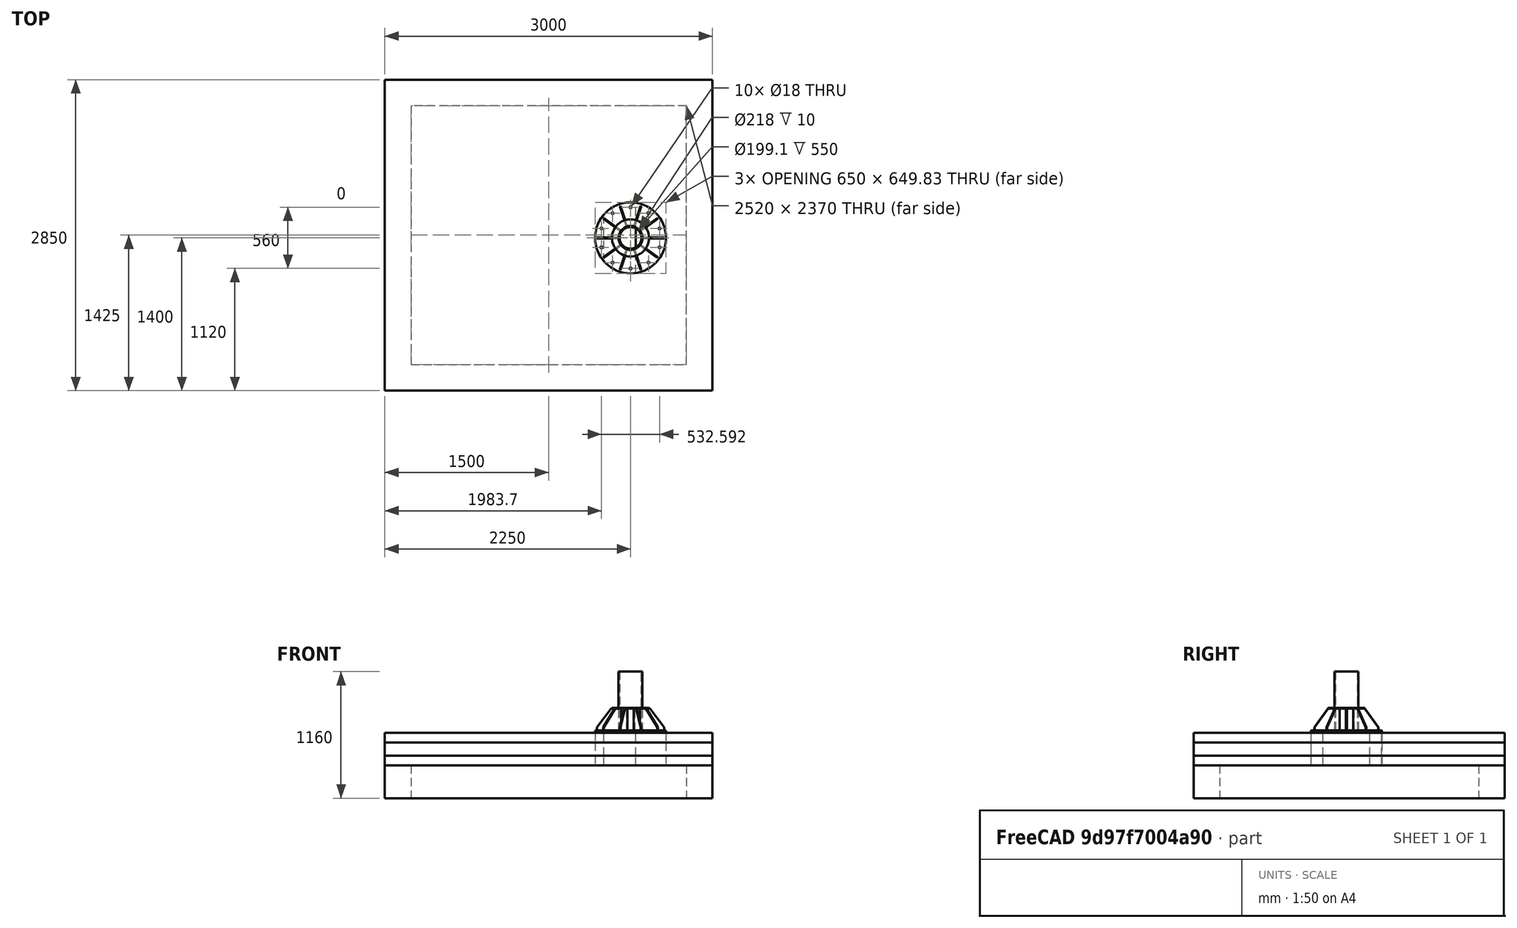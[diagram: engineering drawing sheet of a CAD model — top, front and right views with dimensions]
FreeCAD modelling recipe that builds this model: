
FCSTD DOCUMENT  (FreeCAD 0.21R33694 (Git))
Label: B_Parkaue_LIC_Betonplatte
License: All rights reserved
LicenseURL: http://en.wikipedia.org/wiki/All_rights_reserved
objects: Part::FeaturePython×12, Sketcher::SketchObject×7, Part::Extrusion×7, App::MaterialObjectPython×4, Image::ImagePlane×3, App::DocumentObjectGroup×3, Fem::ConstraintForce×3, Fem::FeaturePython×2, Part::MultiFuse×1, Part::Compound×1, Fem::FemMeshObjectPython×1, Fem::FemSolverObjectPython×1, Fem::ConstraintFixed×1, Fem::FemAnalysis×1
note: 28 computed .brp shape members not serialized (recipe doc carries the construction recipe); baked Part::Feature solids carry a one-line shape summary decoded from their .brp

FEATURE [Sketcher::SketchObject] Sketch
  FullyConstrained = true
  sketch-geometry (3):
    g0: Circle CenterX=0 CenterY=0 CenterZ=0 NormalX=0 NormalY=0 NormalZ=1 AngleXU=0 Radius=109.55
    g1: Circle CenterX=0 CenterY=0 CenterZ=0 NormalX=0 NormalY=0 NormalZ=1 AngleXU=0 Radius=99.55
    g2: LineSegment StartX=99.55 StartY=0 StartZ=0 EndX=109.55 EndY=0 EndZ=0
  constraints (8):
    c: Coincident(g0,g-1)
    c: Diameter(g0) = 219.1
    c: Coincident(g1,g0)
    c: PointOnObject(g2,g1)
    c: PointOnObject(g2,g0)
    c: PointOnObject(g2,g-1)
    c: Horizontal(g2)
    c: DistanceX(g2,g2) = 10
FEATURE [Part::Extrusion] Extrude  label="R219"
  Base = -> Sketch
  Dir = (0,0,1)
  DirMode = 0
  FaceMakerClass = Part::FaceMakerBullseye
  LengthFwd = 550
  LengthRev = 0
  Placement = pos=(0,0,10) rot=(0,0,1;0rad)
  Solid = true
  Symmetric = false
FEATURE [Part::FeaturePython] Flangia  # WARN: FeaturePython — macro-defined, semantics opaque (R4)
  AttacherType = Attacher::AttachEngine3D
  D = 650
  FlangeType = SO
  Kv = 0
  ODp = 0
  PRating = DIN-PN16
  PSize = DN250
  PType = Flange
  Ports = (2) [(0,0,0),(0,0,20)]
  d = 218
  df = 560
  drf = 0
  dwn = 0
  f = 18
  n = 10
  t = 20
  trf = 0
  twn = 0
FEATURE [Sketcher::SketchObject] Sketch002
  ExternalGeometry = -> [Flangia,Extrude]
  FullyConstrained = true
  Placement = pos=(0,0,0) rot=(1,0,0;1.5708rad)
  sketch-geometry (7):
    g0: LineSegment StartX=306.55 StartY=20 StartZ=0 EndX=120.692 EndY=20 EndZ=0
    g1: LineSegment StartX=120.692 StartY=20 StartZ=0 EndX=106.55 EndY=34.1421 EndZ=0
    g2: LineSegment StartX=106.55 StartY=34.1421 StartZ=0 EndX=106.55 EndY=205.858 EndZ=0
    g3: LineSegment StartX=106.55 StartY=205.858 StartZ=0 EndX=120.692 EndY=220 EndZ=0
    g4: LineSegment StartX=120.692 StartY=220 StartZ=0 EndX=176.55 EndY=220 EndZ=0
    g5: LineSegment StartX=176.55 StartY=220 StartZ=0 EndX=306.55 EndY=50 EndZ=0
    g6: LineSegment StartX=306.55 StartY=50 StartZ=0 EndX=306.55 EndY=20 EndZ=0
  constraints (21):
    c: Horizontal(g0)
    c: Coincident(g0,g1)
    c: Coincident(g1,g2)
    c: Vertical(g2)
    c: Coincident(g2,g3)
    c: Coincident(g3,g4)
    c: Horizontal(g4)
    c: Coincident(g4,g5)
    c: Coincident(g5,g6)
    c: Coincident(g6,g0)
    c: Vertical(g6)
    c: Horizontal(g0,g-3)
    c: Angle(g0,g1) = 2.35619
    c: Angle(g3,g4) = 2.35619
    c: Equal(g1,g3)
    c: DistanceX(g1,g-4) = 3
    c: Distance(g3) = 20
    c: DistanceX(g2,g4) = 70
    c: DistanceY(g6,g6) = 30
    c: DistanceY(g0,g4) = 200
    c: DistanceX(g1,g0) = 200
FEATURE [Part::Extrusion] Extrude002
  Base = -> Sketch002
  Dir = (0,-1,2e-16)
  DirMode = 2
  FaceMakerClass = Part::FaceMakerBullseye
  LengthFwd = 8
  LengthRev = 0
  Solid = true
  Symmetric = true
FEATURE [Part::FeaturePython] Array  label="Steifen"  # Draft array (typed FeaturePython)
  Angle = 360
  ArrayType = 1
  Axis = (0,0,1)
  Base = -> Extrude002
  Center = (0,0,0)
  Count = 8
  Fuse = false
  IntervalAxis = (0,0,0)
  IntervalX = (50,0,0)
  IntervalY = (0,50,0)
  IntervalZ = (0,0,50)
  NumberCircles = 3
  NumberPolar = 10
  NumberX = 2
  NumberY = 2
  NumberZ = 1
  RadialDistance = 50
  Symmetry = 1
  TangentialDistance = 25
FEATURE [Sketcher::SketchObject] Sketch003
  FullyConstrained = true
  MapMode = 5
  Placement = pos=(0,4.84e-14,220) rot=(0,0,1;0rad)
  Support = -> [Array]
  sketch-geometry (2):
    g0: Circle CenterX=0 CenterY=0 CenterZ=0 NormalX=0 NormalY=0 NormalZ=1 AngleXU=0 Radius=170
    g1: Circle CenterX=0 CenterY=0 CenterZ=0 NormalX=0 NormalY=0 NormalZ=1 AngleXU=0 Radius=104.5
  constraints (4):
    c: Coincident(g0,g-1)
    c: Coincident(g1,g0)
    c: Diameter(g1) = 209
    c: Diameter(g0) = 340
FEATURE [Part::Extrusion] Extrude003  label="Ringsteife"
  Base = -> Sketch003
  Dir = (0,2e-16,1)
  DirMode = 2
  FaceMakerClass = Part::FaceMakerBullseye
  LengthFwd = 6
  LengthRev = 0
  Solid = true
  Symmetric = false
FEATURE [Part::MultiFuse] Fusion  label="mast_fixing"
  Refine = true
  Shapes = -> [Extrude,Flangia,Array,Extrude003]
FEATURE [Image::ImagePlane] ImagePlane001  label="building"
  Placement = pos=(3085,400,-150) rot=(0,0,1;0rad)
  XSize = 13211.6
  YSize = 11768.8
  expr: XSize = 259.33 * 50.945 mm
  expr: YSize = 231.01 * 50.945 mm
FEATURE [Sketcher::SketchObject] Sketch005
  FullyConstrained = true
  sketch-geometry (4):
    g0: LineSegment StartX=-2250 StartY=1450 StartZ=0 EndX=750 EndY=1450 EndZ=0
    g1: LineSegment StartX=750 StartY=1450 StartZ=0 EndX=750 EndY=-1400 EndZ=0
    g2: LineSegment StartX=750 StartY=-1400 StartZ=0 EndX=-2250 EndY=-1400 EndZ=0
    g3: LineSegment StartX=-2250 StartY=-1400 StartZ=0 EndX=-2250 EndY=1450 EndZ=0
  constraints (12):
    c: Coincident(g0,g1)
    c: Coincident(g1,g2)
    c: Coincident(g2,g3)
    c: Coincident(g3,g0)
    c: Horizontal(g0)
    c: Horizontal(g2)
    c: Vertical(g1)
    c: Vertical(g3)
    c: DistanceX(g2,g2) = 3000
    c: DistanceY(g1,g-1) = 1400
    c: DistanceX(g-1,g1) = 750
    c: DistanceY(g3,g3) = 2850
FEATURE [Part::Extrusion] Extrude005  label="plate"
  Base = -> Sketch005
  Dir = (0,0,-1)
  DirMode = 0
  FaceMakerClass = Part::FaceMakerBullseye
  LengthFwd = 300
  LengthRev = 0
  Solid = true
  Symmetric = false
FEATURE [Sketcher::SketchObject] Sketch006
  FullyConstrained = true
  MapMode = 5
  Support = -> [Extrude005]
  sketch-geometry (7):
    g0: ArcOfCircle CenterX=0 CenterY=0 CenterZ=0 NormalX=0 NormalY=0 NormalZ=1 AngleXU=0 Radius=325 StartAngle=4.85928 EndAngle=7.70709
    g1: LineSegment StartX=0 StartY=0 StartZ=0 EndX=47.5684 EndY=321.5 EndZ=0
    g2: LineSegment StartX=47.5684 StartY=321.5 StartZ=0 EndX=47.5684 EndY=-321.5 EndZ=0
    g3: ArcOfCircle CenterX=0 CenterY=0 CenterZ=0 NormalX=0 NormalY=0 NormalZ=1 AngleXU=0 Radius=325 StartAngle=2.41667 EndAngle=3.86651
    g4: LineSegment StartX=-243.279 StartY=215.5 StartZ=0 EndX=-243.279 EndY=-215.5 EndZ=0
    g5: ArcOfCircle CenterX=0 CenterY=7.85e-14 CenterZ=0 NormalX=0 NormalY=0 NormalZ=1 AngleXU=0 Radius=325 StartAngle=3.86651 EndAngle=4.85928
    g6: ArcOfCircle CenterX=1.314e-13 CenterY=-3.469e-13 CenterZ=0 NormalX=0 NormalY=0 NormalZ=1 AngleXU=0 Radius=325 StartAngle=1.4239 EndAngle=2.41667
  constraints (20):
    c: Coincident(g0,g-1)
    c: Vertical(g0,g0)
    c: Coincident(g1,g0)
    c: Coincident(g1,g0)
    c: Coincident(g2,g0)
    c: Coincident(g2,g0)
    c: Diameter(g0) = 650
    c: Coincident(g3,g0)
    c: Vertical(g3,g3)
    c: Equal(g0,g3)
    c: Coincident(g4,g3)
    c: Coincident(g4,g3)
    c: DistanceY(g2,g2) = 643
    c: DistanceY(g4,g4) = 431
    c: PointOnObject(g5,g-2)
    c: Coincident(g5,g3)
    c: Coincident(g5,g0)
    c: Coincident(g6,g3)
    c: Coincident(g6,g0)
    c: Equal(g6,g0)
FEATURE [Sketcher::SketchObject] Sketch008
  ExternalGeometry = -> [Extrude005]
  FullyConstrained = true
  MapMode = 5
  Placement = pos=(0,0,-300) rot=(1,0,0;3.14159rad)
  Support = -> [Extrude005]
  sketch-geometry (12):
    g0: LineSegment StartX=-2250 StartY=1400 StartZ=0 EndX=750 EndY=1400 EndZ=0
    g1: LineSegment StartX=750 StartY=1400 StartZ=0 EndX=750 EndY=-1450 EndZ=0
    g2: LineSegment StartX=750 StartY=-1450 StartZ=0 EndX=-2250 EndY=-1450 EndZ=0
    g3: LineSegment StartX=-2250 StartY=-1450 StartZ=0 EndX=-2250 EndY=1400 EndZ=0
    g4: LineSegment StartX=-2010 StartY=1160 StartZ=0 EndX=510 EndY=1160 EndZ=0
    g5: LineSegment StartX=510 StartY=1160 StartZ=0 EndX=510 EndY=-1210 EndZ=0
    g6: LineSegment StartX=510 StartY=-1210 StartZ=0 EndX=-2010 EndY=-1210 EndZ=0
    g7: LineSegment StartX=-2010 StartY=-1210 StartZ=0 EndX=-2010 EndY=1160 EndZ=0
    g8: LineSegment StartX=-2010 StartY=1160 StartZ=0 EndX=-2010 EndY=1400 EndZ=0
    g9: LineSegment StartX=510 StartY=1160 StartZ=0 EndX=750 EndY=1160 EndZ=0
    g10: LineSegment StartX=-2010 StartY=-1210 StartZ=0 EndX=-2010 EndY=-1450 EndZ=0
    g11: LineSegment StartX=-2010 StartY=1160 StartZ=0 EndX=-2250 EndY=1160 EndZ=0
  constraints (34):
    c: Coincident(g0,g1)
    c: Coincident(g1,g2)
    c: Coincident(g2,g3)
    c: Coincident(g3,g0)
    c: Horizontal(g0)
    c: Horizontal(g2)
    c: Vertical(g1)
    c: Vertical(g3)
    c: Coincident(g0,g-3)
    c: Coincident(g1,g-4)
    c: Coincident(g4,g5)
    c: Coincident(g5,g6)
    c: Coincident(g6,g7)
    c: Coincident(g7,g4)
    c: Horizontal(g4)
    c: Horizontal(g6)
    c: Vertical(g5)
    c: Vertical(g7)
    c: Coincident(g8,g4)
    c: PointOnObject(g8,g0)
    c: Vertical(g8)
    c: Coincident(g9,g4)
    c: PointOnObject(g9,g1)
    c: Horizontal(g9)
    c: Equal(g8,g9)
    c: Coincident(g10,g6)
    c: PointOnObject(g10,g2)
    c: Vertical(g10)
    c: Coincident(g11,g4)
    c: PointOnObject(g11,g3)
    c: Horizontal(g11)
    c: Equal(g11,g8)
    c: Equal(g9,g10)
    c: DistanceX(g9,g9) = 240
FEATURE [Part::Extrusion] Extrude009  label="wall_masonry"
  Base = -> Sketch008
  Dir = (0,0,-1)
  DirMode = 2
  FaceMakerClass = Part::FaceMakerBullseye
  LengthFwd = 300
  LengthRev = 0
  Solid = true
  Symmetric = false
FEATURE [Image::ImagePlane] ImagePlane  label="top_view"
  Placement = pos=(32,-830,-100) rot=(0,0,1;0rad)
  XSize = 5389.33
  YSize = 4906.39
  expr: XSize = 206.67 * 26.077 mm
  expr: YSize = 188.15 * 26.077 mm
FEATURE [Image::ImagePlane] ImagePlane002  label="ansicht_yz"
  Placement = pos=(-2572,-300,2633) rot=(0.57735,0.57735,0.57735;2.0944rad)
  XSize = 4807.43
  YSize = 6945.54
  expr: XSize = 184.44 * 26.065 mm
  expr: YSize = 266.47 * 26.065 mm
FEATURE [App::DocumentObjectGroup] Group  label="drawings"
  Group = -> [ImagePlane001,ImagePlane,ImagePlane002]
FEATURE [Part::Extrusion] Extrude010  label="slice_loadFaces"
  Base = -> Sketch006
  Dir = (0,0,1)
  DirMode = 2
  FaceMakerClass = Part::FaceMakerBullseye
  LengthFwd = 100
  LengthRev = 400
  Solid = false
  Symmetric = false
FEATURE [Sketcher::SketchObject] Sketch009
  ExternalGeometry = -> [Extrude005]
  FullyConstrained = true
  Placement = pos=(0,0,0) rot=(1,0,0;1.5708rad)
  sketch-geometry (6):
    g0: LineSegment StartX=-2250 StartY=-45 StartZ=0 EndX=750 EndY=-45 EndZ=0
    g1: LineSegment StartX=-2250 StartY=-255 StartZ=0 EndX=750 EndY=-255 EndZ=0
    g2: LineSegment StartX=-2350 StartY=-210 StartZ=0 EndX=850 EndY=-210 EndZ=0
    g3: LineSegment StartX=-2350 StartY=-90 StartZ=0 EndX=850 EndY=-90 EndZ=0
    g4: LineSegment StartX=750 StartY=-255 StartZ=0 EndX=850 EndY=-210 EndZ=0
    g5: LineSegment StartX=750 StartY=-45 StartZ=0 EndX=850 EndY=-90 EndZ=0
  constraints (20):
    c: Horizontal(g0)
    c: Horizontal(g1)
    c: PointOnObject(g0,g-4)
    c: PointOnObject(g1,g-4)
    c: PointOnObject(g0,g-3)
    c: PointOnObject(g1,g-3)
    c: DistanceY(g-3,g1) = 45
    c: DistanceY(g0,g-3) = 45
    c: Horizontal(g2)
    c: Horizontal(g3)
    c: Equal(g3,g2)
    c: Vertical(g2,g3)
    c: DistanceX(g3,g-4) = 100
    c: DistanceX(g-3,g3) = 100
    c: Coincident(g4,g1)
    c: Coincident(g4,g2)
    c: Coincident(g5,g0)
    c: Coincident(g5,g3)
    c: Equal(g4,g5)
    c: DistanceY(g1,g2) = 45
FEATURE [Part::Extrusion] Extrude011  label="slice_Q524"
  Base = -> Sketch009
  Dir = (0,-1,-3e-16)
  DirMode = 2
  FaceMakerClass = Part::FaceMakerBullseye
  LengthFwd = 3200
  LengthRev = 0
  Solid = false
  Symmetric = true
FEATURE [Part::FeaturePython] Slice  # WARN: FeaturePython — macro-defined, semantics opaque (R4)
  Base = -> Extrude005
  Mode = 1
  Tolerance = 0
  Tools = -> [Extrude010]
FEATURE [Part::FeaturePython] Slice_child0  label="plate_rest_not_used"  # WARN: FeaturePython — macro-defined, semantics opaque (R4)
  Base = -> Slice
  FilterType = 1
  Invert = false
  OverrideMaxVal = 0
  WindowFrom = 80
  WindowTo = 100
  items = 0
FEATURE [Part::FeaturePython] Slice_child1  label="mast_neutral"  # WARN: FeaturePython — macro-defined, semantics opaque (R4)
  Base = -> Slice
  FilterType = 1
  Invert = false
  OverrideMaxVal = 0
  WindowFrom = 80
  WindowTo = 100
  items = 1
FEATURE [Part::FeaturePython] Slice_child2  label="mast_Z"  # WARN: FeaturePython — macro-defined, semantics opaque (R4)
  Base = -> Slice
  FilterType = 1
  Invert = false
  OverrideMaxVal = 0
  WindowFrom = 80
  WindowTo = 100
  items = 2
FEATURE [Part::FeaturePython] Slice_child3  label="mast_D"  # WARN: FeaturePython — macro-defined, semantics opaque (R4)
  Base = -> Slice
  FilterType = 1
  Invert = false
  OverrideMaxVal = 0
  WindowFrom = 80
  WindowTo = 100
  items = 3
FEATURE [App::DocumentObjectGroup] GrExplode_Slice  label="Exploded Slice"
  Group = -> [Slice_child0,Slice_child1,Slice_child2,Slice_child3]
FEATURE [Part::FeaturePython] Slice001  # WARN: FeaturePython — macro-defined, semantics opaque (R4)
  Base = -> Slice_child0
  Mode = 1
  Tolerance = 0
  Tools = -> [Extrude011]
FEATURE [Part::FeaturePython] Slice001_child0  label="plate_up"  # WARN: FeaturePython — macro-defined, semantics opaque (R4)
  Base = -> Slice001
  FilterType = 1
  Invert = false
  OverrideMaxVal = 0
  WindowFrom = 80
  WindowTo = 100
  items = 0
FEATURE [Part::FeaturePython] Slice001_child1  label="plate_middle"  # WARN: FeaturePython — macro-defined, semantics opaque (R4)
  Base = -> Slice001
  FilterType = 1
  Invert = false
  OverrideMaxVal = 0
  WindowFrom = 80
  WindowTo = 100
  items = 1
FEATURE [Part::FeaturePython] Slice001_child2  label="plate_bottom"  # WARN: FeaturePython — macro-defined, semantics opaque (R4)
  Base = -> Slice001
  FilterType = 1
  Invert = false
  OverrideMaxVal = 0
  WindowFrom = 80
  WindowTo = 100
  items = 2
FEATURE [App::DocumentObjectGroup] GrExplode_Slice001  label="Exploded Slice001"
  Group = -> [Slice001_child0,Slice001_child1,Slice001_child2]
FEATURE [Part::FeaturePython] BooleanFragments  # WARN: FeaturePython — macro-defined, semantics opaque (R4)
  Mode = 2
  Objects = -> [Extrude009,Slice_child1,Slice_child2,Slice_child3,Slice001_child0,Slice001_child1,Slice001_child2]
  Tolerance = 0
FEATURE [Part::Compound] Compound
  Links = -> [BooleanFragments]
FEATURE [Fem::FeaturePython] MeshRegion  # FEM object (typed FeaturePython)
  CharacteristicLength = 50
  References = -> [Compound]
FEATURE [Fem::FeaturePython] MeshRegion001  # FEM object (typed FeaturePython)
  CharacteristicLength = 100
  References = -> [Compound]
FEATURE [Fem::FemMeshObjectPython] FEMMeshGmsh  # FEM object (typed FeaturePython)
  Algorithm2D = 0
  Algorithm3D = 0
  CharacteristicLengthMax = 500
  CharacteristicLengthMin = 0
  CoherenceMesh = true
  ElementDimension = 3
  ElementOrder = 1
  GeometryTolerance = 1e-06
  GroupsOfNodes = false
  HighOrderOptimize = 0
  MeshRegionList = -> [MeshRegion,MeshRegion001]
  MeshSizeFromCurvature = 12
  OptimizeNetgen = false
  OptimizeStd = true
  Part = -> Compound
  RecombinationAlgorithm = 0
  Recombine3DAll = false
  RecombineAll = false
  SecondOrderLinear = false
FEATURE [Fem::FemSolverObjectPython] SolverCcxTools  # FEM object (typed FeaturePython)
  AnalysisType = 0
  BeamShellResultOutput3D = true
  BucklingFactors = 1
  EigenmodeHighLimit = 1000000
  EigenmodeLowLimit = 0
  EigenmodesCount = 10
  GeometricalNonlinearity = 0
  IterationsControlParameterCutb = 0.25,0.5,0.75,0.85,,,1.5,
  IterationsControlParameterIter = 4,8,9,200,10,400,,200,,
  IterationsControlParameterTimeUse = false
  IterationsThermoMechMaximum = 2000
  IterationsUserDefinedIncrementations = false
  IterationsUserDefinedTimeStepLength = false
  MaterialNonlinearity = 0
  MatrixSolverType = 0
  SplitInputWriter = true
  ThermoMechSteadyState = true
  TimeEnd = 1
  TimeInitialStep = 0.01
FEATURE [App::MaterialObjectPython] MaterialSolid  label="plate_0.006"  # material (typed FeaturePython)
  Category = 0
  Material = AngleOfFriction=30 deg,AuthorAndLicense=(c) 2019 Bernd Hahnebach (CC-BY 3.0),CardName=Concrete-EN-C35_45,CompressiveStrength=15.75 MPa,+7 more (map truncated)
  References = -> [Slice001_child0,Slice001_child2]
FEATURE [App::MaterialObjectPython] MaterialSolid001  label="plate_0.001"  # material (typed FeaturePython)
  Category = 0
  Material = AngleOfFriction=30 deg,AuthorAndLicense=(c) 2019 Bernd Hahnebach (CC-BY 3.0),CardName=Concrete-EN-C35_45,CompressiveStrength=15.75 MPa,+7 more (map truncated)
  References = -> [Slice001_child1]
FEATURE [App::MaterialObjectPython] MaterialSolid002  label="wall_0.001"  # material (typed FeaturePython)
  Category = 0
  Material = AuthorAndLicense=(c) 2013 Yorik van Havre (CC-BY 3.0),CardName=Concrete-Generic,CompressiveStrength=25 MPa,Density=1800.0 kg/m^3,+7 more (map truncated)
  References = -> [Extrude009]
FEATURE [App::MaterialObjectPython] MaterialSolid003  label="mast"  # material (typed FeaturePython)
  Category = 0
  Material = AngleOfFriction=30 deg,AuthorAndLicense=(c) 2019 Bernd Hahnebach (CC-BY 3.0),CardName=Concrete-EN-C35_45,CompressiveStrength=15.75 MPa,+7 more (map truncated)
  References = -> [Slice_child3,Slice_child1,Slice_child2]
FEATURE [Fem::ConstraintFixed] ConstraintFixed
  NormalDirection = (0,0,-1)
  Normals = (24) [(0,0,-1),(0,0,-1),(0,0,-1),(0,0,-1),(0,0,-1),(0,0,-1),(0,0,-1),(0,0,-1),(0,0,-1),(0,0,-1),(0,0,-1),(0,0,-1),(0,0,-1),(0,0,-1),(0,0,-1),(0,0,-1),+8 more]
  Points = (24) [(-2250,-1400,-600),(-1750,-1400,-600),(-1250,-1400,-600),(-750,-1400,-600),(-250,-1400,-600),(250,-1400,-600),(750,-1400,-600),(-2250,-925,-600),+16 more]
  References = -> [Compound]
  Scale = 51
FEATURE [Fem::ConstraintForce] ConstraintForce  label="mastZ"
  DirectionVector = (0,0,1)
  Force = 85000
  NormalDirection = (0,0,-1)
  Points = (8) [(47.5684,-321.5,-300),(47.5684,-107.167,-300),(140.046,-107.167,-300),(232.523,-107.167,-300),(47.5684,107.167,-300),(140.046,107.167,-300),+2 more]
  References = -> [Slice_child2]
  Reversed = true
  Scale = 23
FEATURE [Fem::ConstraintForce] ConstraintForce001  label="mastD"
  DirectionVector = (0,0,-1)
  Force = 85000
  NormalDirection = (0,0,1)
  Points = (8) [(-243.279,-215.5,0),(-297.76,-71.8333,0),(-270.519,-71.8333,0),(-243.279,-71.8333,0),(-297.76,71.8333,0),(-270.519,71.8333,0),(-243.279,71.8333,0),+1 more]
  References = -> [Compound]
  Reversed = true
  Scale = 17
FEATURE [Fem::ConstraintForce] ConstraintForce002  label="mastN(p)"
  DirectionVector = (0,0,-1)
  Force = 9800
  NormalDirection = (0,0,1)
  Points = (24) [(-243.279,-215.5,0),(-297.76,-71.8333,0),(-270.519,-71.8333,0),(-243.279,-71.8333,0),(-297.76,71.8333,0),(-270.519,71.8333,0),(-243.279,71.8333,0),+17 more]
  References = -> [Compound]
  Reversed = true
  Scale = 23
FEATURE [Fem::FemAnalysis] Analysis
  Group = -> [SolverCcxTools,MaterialSolid,MaterialSolid001,MaterialSolid002,MaterialSolid003,ConstraintFixed,ConstraintForce,ConstraintForce001,ConstraintForce002,FEMMeshGmsh]
